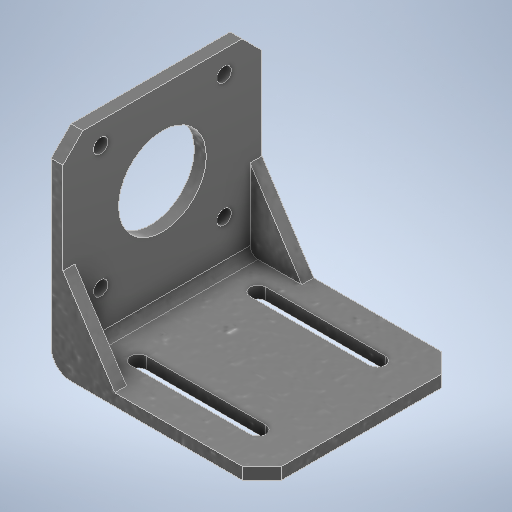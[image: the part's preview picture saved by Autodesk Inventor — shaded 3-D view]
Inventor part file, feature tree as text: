
AUTODESK INVENTOR PART (.ipt)
format: ipt  version: 2025.2 (Build 292293000, 293)  size: 371,200 bytes
history: native  units: in
note: dims shown in document units (in); Inventor stores cm internally (conversion verified against a paired STEP export)
features: mirror x1
ambient origin geometry x8: Origin, YZ Plane, XZ Plane, XY Plane, X Axis, Y Axis, Z Axis, Center Point
bodies: Solid1 (feature_tree)
feature tree (1):
  mirror  "Mirror1"
